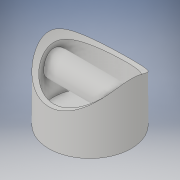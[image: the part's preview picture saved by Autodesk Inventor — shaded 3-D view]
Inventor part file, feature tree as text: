
AUTODESK INVENTOR PART (.ipt)
format: ipt  version: 2018 (Build 220112000, 112)  size: 184,320 bytes
history: native  units: in
note: dims shown in document units (in); Inventor stores cm internally (conversion verified against a paired STEP export)
features: extrude x8, sketch x8, plane x2, mirror x1, projected_geometry x1
ambient origin geometry x8: Origin, YZ Plane, XZ Plane, XY Plane, X Axis, Y Axis, Z Axis, Center Point
bodies: Solid1 (feature_tree)
feature tree (20):
  extrude  "Extrusion1"  Depth=2.5in TaperAngle=0.0deg
  extrude  "Extrusion2"  Depth=1.5in TaperAngle=0.0deg
  plane  "Work Plane1"
  extrude  "Extrusion3"  Depth=3.0in
  extrude  "Extrusion4"  Depth=1.0in
  extrude  "Extrusion5"  TaperAngle=0.0deg  [1 undecoded]
  extrude  "Extrusion6"  Depth=1.1in
  plane  "Work Plane2"
  extrude  "Extrusion7"  Depth=1.5in
  mirror  "Mirror1"
  extrude  "Extrusion8"  Depth=1.5in
  sketch  "Sketch1"  dims[d0=3.4in d1=2.5in d2=0.0in]
  sketch  "Sketch2"  dims[d4=1.5in d5=4.0in d6=0.0in]
  sketch  "Sketch3"  dims[d7=-2.5in d8=3.0in]
  sketch  "Sketch4"  dims[d9=2.25in d10=0.0in d11=1.0in]
  sketch  "Sketch5"  dims[d12=1.0in d13=0.0in]
  sketch  "Sketch6"  dims[d14=3.1in d15=0.0in d16=1.1in]
  sketch  "Sketch7"  dims[d17=1.35in d18=1.5in]
  sketch  "Sketch8"  dims[d19=1.7in d20=1.6in d21=0.0in d22=4.7in d23=2.0in d24=1.25in d25=0.0in d26=100.0in d27=0.0in d28=-0.9in d29=0.2in d30=0.25in d31=0.0in d32=1.5in d33=0.0in]
  projected_geometry  "Projected Loop1"
note: 1 required parameter value undecoded (feature->parameter linkage not recoverable at this tier; creation-order binding heuristic only, values carry confidence <= 0.55)
